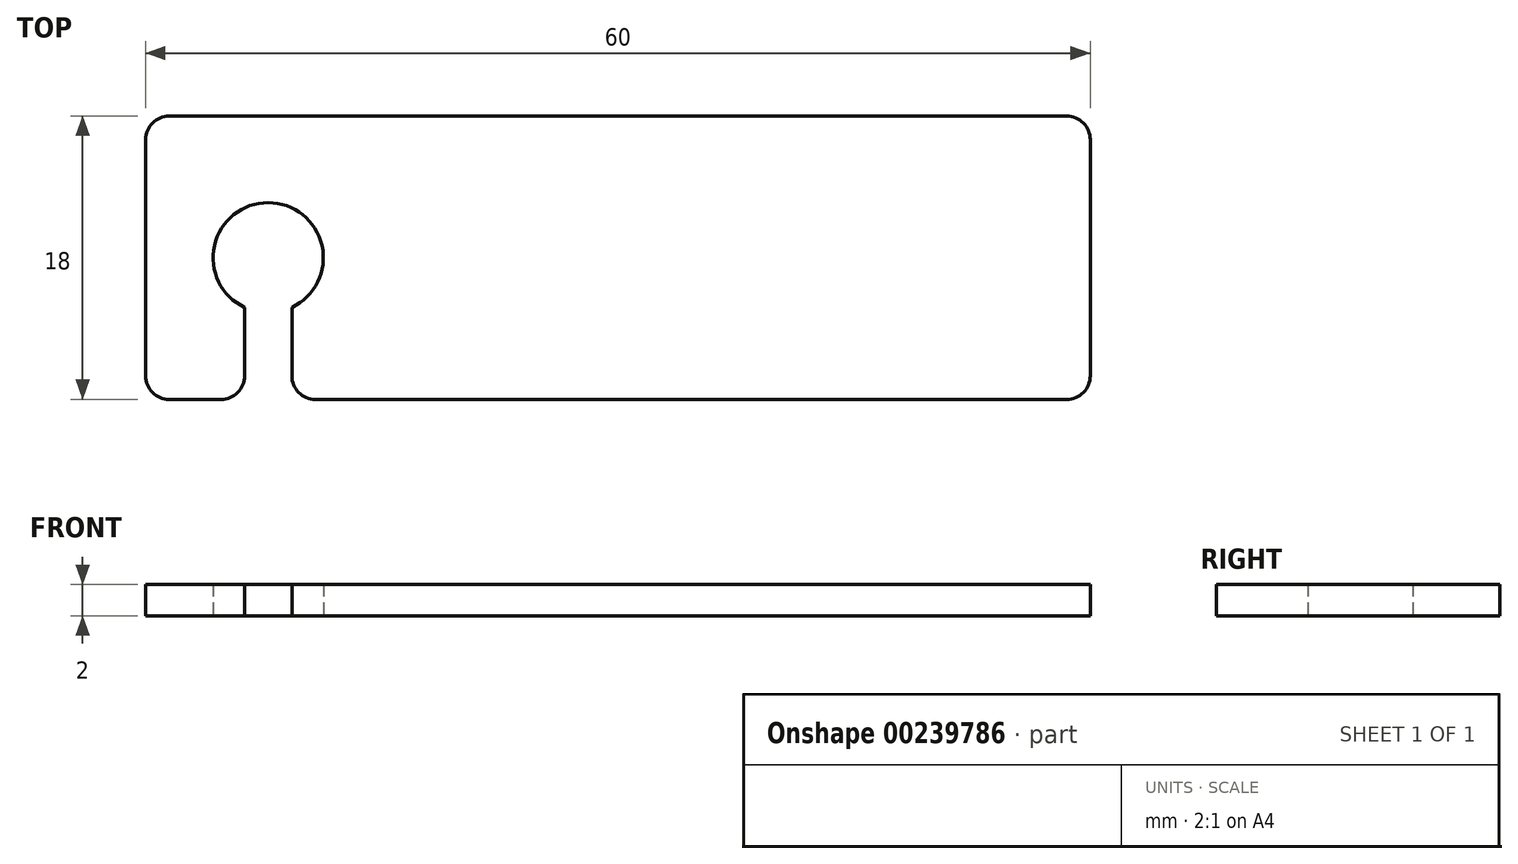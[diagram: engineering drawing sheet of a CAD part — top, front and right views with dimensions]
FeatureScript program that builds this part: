
annotation { "Feature Type Name" : "Feature", "Feature Type Description" : "" }
export const myFeature = defineFeature(function(context is Context, id is Id, definition is map)
    precondition{}
    {
        {
            var Q0;
            Q0=qCreatedBy(makeId("Top.planeOp"),FACE);
            var sketch = newSketch(context, id + "F0", { "sketchPlane" : qUnion([Q0])});
            skLineSegment(sketch, "E0.bottom", {"start": v(30, -9) * mm, "end": v(-20.7, -9) * mm});
            skLineSegment(sketch, "E0.top", {"start": v(30, 9) * mm, "end": v(-30, 9) * mm});
            skLineSegment(sketch, "E0.left", {"start": v(30, -9) * mm, "end": v(30, 9) * mm});
            skLineSegment(sketch, "E0.right", {"start": v(-30, -9) * mm, "end": v(-30, 9) * mm});
            skPoint(sketch, "E0.middle", {"position": v(0, 0) * mm});
            skPoint(sketch, "E1.endSnap0", {"position": v(-30, 0) * mm});
            skArc(sketch, "E2", {"start": v(-20.7, -3.16) * mm, "mid": v(-22.2, 3.5) * mm, "end": v(-23.7, -3.16) * mm});
            skLineSegment(sketch, "E3", {"start": v(-23.7, -3.16) * mm, "end": v(-23.7, -9) * mm});
            skLineSegment(sketch, "E4", {"start": v(-20.7, -3.16) * mm, "end": v(-20.7, -9) * mm});
            skPoint(sketch, "E5.end.orphan", {"position": v(-22.2, -9) * mm});
            skLineSegment(sketch, "E6.trimOffspring", {"start": v(-23.7, -9) * mm, "end": v(-30, -9) * mm});
            skSolve(sketch);
        }
        {
            var Q0;
            Q0=makeQuery(id+"F0.imprint","IMPRINT",FACE,{"disambiguationData":[TD([[makeQuery(id+"F0.imprint","IMPRINT",EDGE,{"derivedFrom":sQuery(id+"F0.wireOp",EDGE,"E0.bottom")}),-1.0]])]});
            extrude(context, id + "F1", {"entities" : qUnion([Q0]), "depth" : 2 * mm});
        }
        {
            var Q0;
            Q0=makeQuery(id+"F1.opExtrude","SWEPT_EDGE",EDGE,{"disambiguationData":[OSD([sQuery(id+"F0.wireOp",EDGE,"E0.bottom"),sQuery(id+"F0.wireOp",EDGE,"E0.left")])]});
            var Q1;
            Q1=makeQuery(id+"F1.opExtrude","SWEPT_EDGE",EDGE,{"disambiguationData":[OSD([sQuery(id+"F0.wireOp",EDGE,"E0.top"),sQuery(id+"F0.wireOp",EDGE,"E0.left")])]});
            var Q2;
            Q2=makeQuery(id+"F1.opExtrude","SWEPT_EDGE",EDGE,{"disambiguationData":[OSD([sQuery(id+"F0.wireOp",EDGE,"E0.right"),sQuery(id+"F0.wireOp",EDGE,"E6.trimOffspring")])]});
            var Q3;
            Q3=makeQuery(id+"F1.opExtrude","SWEPT_EDGE",EDGE,{"disambiguationData":[OSD([sQuery(id+"F0.wireOp",EDGE,"E0.top"),sQuery(id+"F0.wireOp",EDGE,"E0.right")])]});
            var Q4;
            Q4=makeQuery(id+"F1.opExtrude","SWEPT_EDGE",EDGE,{"disambiguationData":[OSD([sQuery(id+"F0.wireOp",EDGE,"E3"),sQuery(id+"F0.wireOp",EDGE,"E6.trimOffspring")])]});
            var Q5;
            Q5=makeQuery(id+"F1.opExtrude","SWEPT_EDGE",EDGE,{"disambiguationData":[OSD([sQuery(id+"F0.wireOp",EDGE,"E0.bottom"),sQuery(id+"F0.wireOp",EDGE,"E4")])]});
            fillet(context, id + "F2", {"entities" : qUnion([Q0, Q1, Q2, Q3, Q4, Q5]), "radius" : 1.5 * mm, "tangentPropagation" : true, "allowEdgeOverflow" : false});
        }
    });
